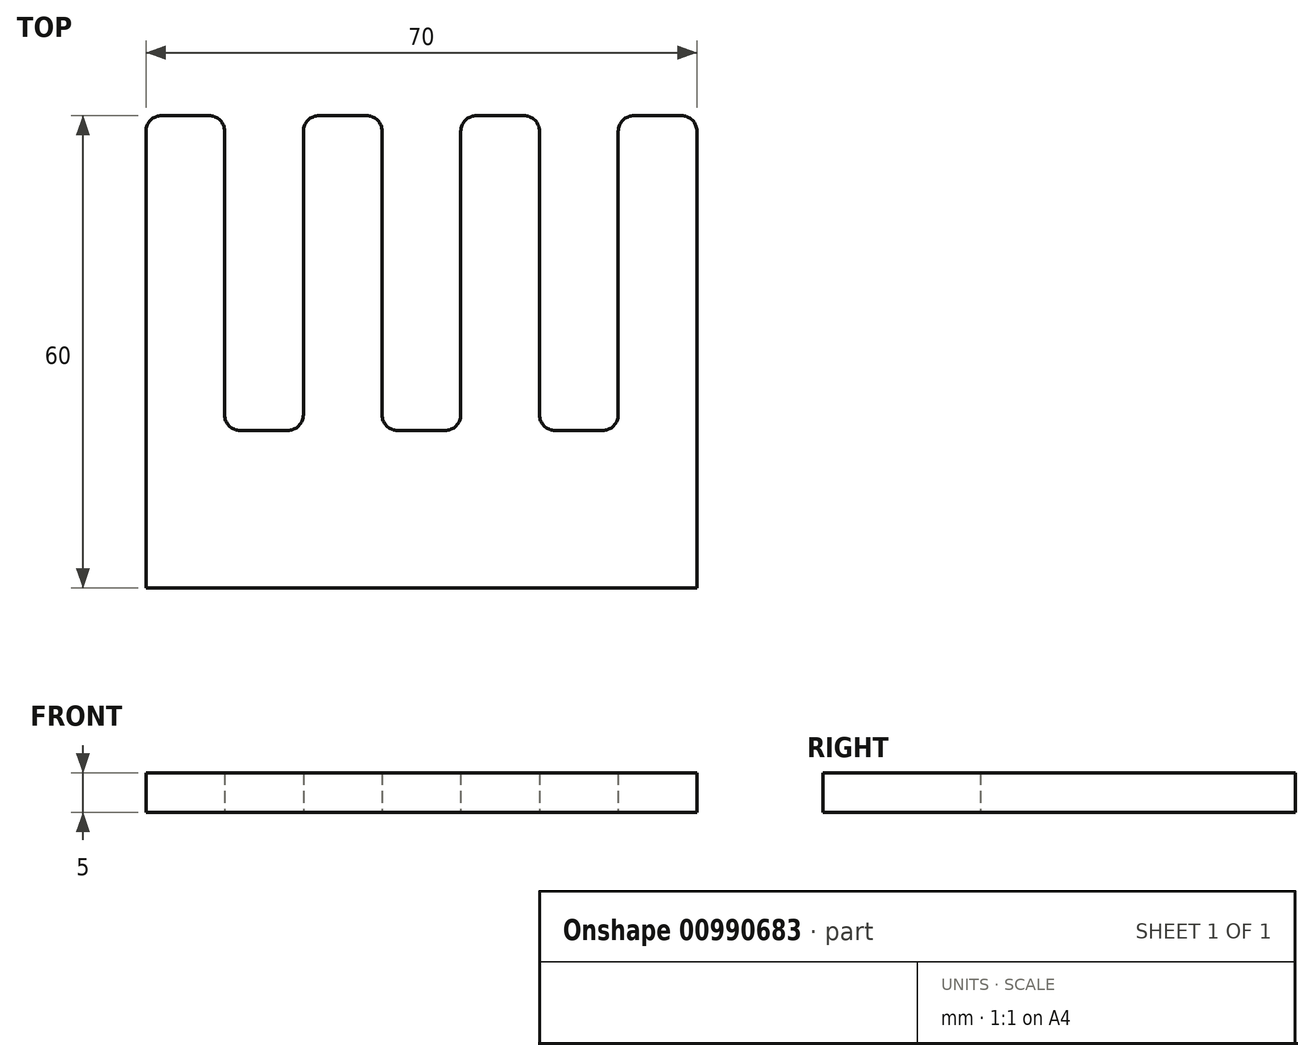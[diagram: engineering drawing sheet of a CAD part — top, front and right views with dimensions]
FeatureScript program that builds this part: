
annotation { "Feature Type Name" : "Feature", "Feature Type Description" : "" }
export const myFeature = defineFeature(function(context is Context, id is Id, definition is map)
    precondition{}
    {
        {
            var Q0;
            Q0=qCreatedBy(makeId("Top.planeOp"),FACE);
            var sketch = newSketch(context, id + "F0", { "sketchPlane" : qUnion([Q0])});
            skLineSegment(sketch, "E0", {"start": v(0, 0) * mm, "end": v(70, 0) * mm});
            skLineSegment(sketch, "E1", {"start": v(70, 0) * mm, "end": v(70, 60) * mm});
            skLineSegment(sketch, "E2", {"start": v(70, 60) * mm, "end": v(60, 60) * mm});
            skLineSegment(sketch, "E3", {"start": v(60, 60) * mm, "end": v(60, 20) * mm});
            skLineSegment(sketch, "E4", {"start": v(60, 20) * mm, "end": v(50, 20) * mm});
            skLineSegment(sketch, "E5", {"start": v(50, 20) * mm, "end": v(50, 60) * mm});
            skLineSegment(sketch, "E6", {"start": v(50, 60) * mm, "end": v(40, 60) * mm});
            skLineSegment(sketch, "E7", {"start": v(40, 60) * mm, "end": v(40, 20) * mm});
            skLineSegment(sketch, "E8", {"start": v(40, 20) * mm, "end": v(30, 20) * mm});
            skLineSegment(sketch, "E9", {"start": v(30, 20) * mm, "end": v(30, 60) * mm});
            skLineSegment(sketch, "E10", {"start": v(30, 60) * mm, "end": v(20, 60) * mm});
            skLineSegment(sketch, "E11", {"start": v(20, 60) * mm, "end": v(20, 20) * mm});
            skLineSegment(sketch, "E12", {"start": v(20, 20) * mm, "end": v(10, 20) * mm});
            skLineSegment(sketch, "E13", {"start": v(10, 20) * mm, "end": v(10, 60) * mm});
            skLineSegment(sketch, "E14", {"start": v(10, 60) * mm, "end": v(0, 60) * mm});
            skLineSegment(sketch, "E15", {"start": v(0, 60) * mm, "end": v(0, 0) * mm});
            skSolve(sketch);
        }
        {
            var Q0;
            Q0=makeQuery(id+"F0.imprint","IMPRINT",FACE,{"disambiguationData":[TD([[makeQuery(id+"F0.imprint","IMPRINT",EDGE,{"derivedFrom":sQuery(id+"F0.wireOp",EDGE,"E0")}),1.0]])]});
            extrude(context, id + "F1", {"entities" : qUnion([Q0]), "depth" : 5 * mm, "offsetDistance" : 25 * mm});
        }
        {
            var Q0;
            Q0=makeQuery(id+"F1.opExtrude","SWEPT_EDGE",EDGE,{"disambiguationData":[OSD([sQuery(id+"F0.wireOp",EDGE,"E13"),sQuery(id+"F0.wireOp",EDGE,"E14")])]});
            var Q1;
            Q1=makeQuery(id+"F1.opExtrude","SWEPT_EDGE",EDGE,{"disambiguationData":[OSD([sQuery(id+"F0.wireOp",EDGE,"E14"),sQuery(id+"F0.wireOp",EDGE,"E15")])]});
            var Q2;
            Q2=makeQuery(id+"F1.opExtrude","SWEPT_EDGE",EDGE,{"disambiguationData":[OSD([sQuery(id+"F0.wireOp",EDGE,"E10"),sQuery(id+"F0.wireOp",EDGE,"E11")])]});
            var Q3;
            Q3=makeQuery(id+"F1.opExtrude","SWEPT_EDGE",EDGE,{"disambiguationData":[OSD([sQuery(id+"F0.wireOp",EDGE,"E9"),sQuery(id+"F0.wireOp",EDGE,"E10")])]});
            var Q4;
            Q4=makeQuery(id+"F1.opExtrude","SWEPT_EDGE",EDGE,{"disambiguationData":[OSD([sQuery(id+"F0.wireOp",EDGE,"E6"),sQuery(id+"F0.wireOp",EDGE,"E7")])]});
            var Q5;
            Q5=makeQuery(id+"F1.opExtrude","SWEPT_EDGE",EDGE,{"disambiguationData":[OSD([sQuery(id+"F0.wireOp",EDGE,"E5"),sQuery(id+"F0.wireOp",EDGE,"E6")])]});
            var Q6;
            Q6=makeQuery(id+"F1.opExtrude","SWEPT_EDGE",EDGE,{"disambiguationData":[OSD([sQuery(id+"F0.wireOp",EDGE,"E2"),sQuery(id+"F0.wireOp",EDGE,"E3")])]});
            var Q7;
            Q7=makeQuery(id+"F1.opExtrude","SWEPT_EDGE",EDGE,{"disambiguationData":[OSD([sQuery(id+"F0.wireOp",EDGE,"E1"),sQuery(id+"F0.wireOp",EDGE,"E2")])]});
            var Q8;
            Q8=makeQuery(id+"F1.opExtrude","SWEPT_EDGE",EDGE,{"disambiguationData":[OSD([sQuery(id+"F0.wireOp",EDGE,"E12"),sQuery(id+"F0.wireOp",EDGE,"E13")])]});
            var Q9;
            Q9=makeQuery(id+"F1.opExtrude","SWEPT_EDGE",EDGE,{"disambiguationData":[OSD([sQuery(id+"F0.wireOp",EDGE,"E11"),sQuery(id+"F0.wireOp",EDGE,"E12")])]});
            var Q10;
            Q10=makeQuery(id+"F1.opExtrude","SWEPT_EDGE",EDGE,{"disambiguationData":[OSD([sQuery(id+"F0.wireOp",EDGE,"E8"),sQuery(id+"F0.wireOp",EDGE,"E9")])]});
            var Q11;
            Q11=makeQuery(id+"F1.opExtrude","SWEPT_EDGE",EDGE,{"disambiguationData":[OSD([sQuery(id+"F0.wireOp",EDGE,"E7"),sQuery(id+"F0.wireOp",EDGE,"E8")])]});
            var Q12;
            Q12=makeQuery(id+"F1.opExtrude","SWEPT_EDGE",EDGE,{"disambiguationData":[OSD([sQuery(id+"F0.wireOp",EDGE,"E4"),sQuery(id+"F0.wireOp",EDGE,"E5")])]});
            var Q13;
            Q13=makeQuery(id+"F1.opExtrude","SWEPT_EDGE",EDGE,{"disambiguationData":[OSD([sQuery(id+"F0.wireOp",EDGE,"E3"),sQuery(id+"F0.wireOp",EDGE,"E4")])]});
            fillet(context, id + "F2", {"entities" : qUnion([Q0, Q1, Q2, Q3, Q4, Q5, Q6, Q7, Q8, Q9, Q10, Q11, Q12, Q13]), "radius" : 2 * mm, "tangentPropagation" : true, "allowEdgeOverflow" : false});
        }
    });
